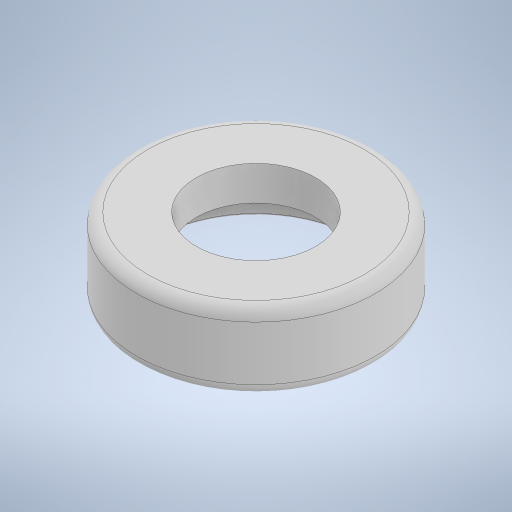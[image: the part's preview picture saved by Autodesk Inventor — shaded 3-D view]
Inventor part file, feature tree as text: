
AUTODESK INVENTOR PART (.ipt)
format: ipt  version: 2024 (Build 280153000, 153)  size: 269,824 bytes
history: native  units: in
note: dims shown in document units (in); Inventor stores cm internally (conversion verified against a paired STEP export)
features: sketch x2, revolve x1, fillet x1, extrude x1, direct_edit x1, other x1
ambient origin geometry x8: Origin, YZ Plane, XZ Plane, XY Plane, X Axis, Y Axis, Z Axis, Center Point
bodies: Solid1 (feature_tree)
feature tree (7):
  revolve  "Revolution1"  [1 undecoded]
  fillet  "Fillet1"  Radius=0.1625in
  extrude  "Extrusion1"  TaperAngle=90.0deg  [1 undecoded]
  direct_edit  "Direct Edit1"
  sketch  "Sketch1"  dims[d0=0.1625in d1=0.025in d2=0.1625in]
  sketch  "Sketch2"  dims[d3=0.1875in d4=90.0deg d5=0.015in d6=0.1625in d7=0.0in d8=0.0in d9=3.937in d10=0.3937in d11=0.3937in]
  other  "Scale1"
note: 2 required parameter values undecoded (feature->parameter linkage not recoverable at this tier; creation-order binding heuristic only, values carry confidence <= 0.55)